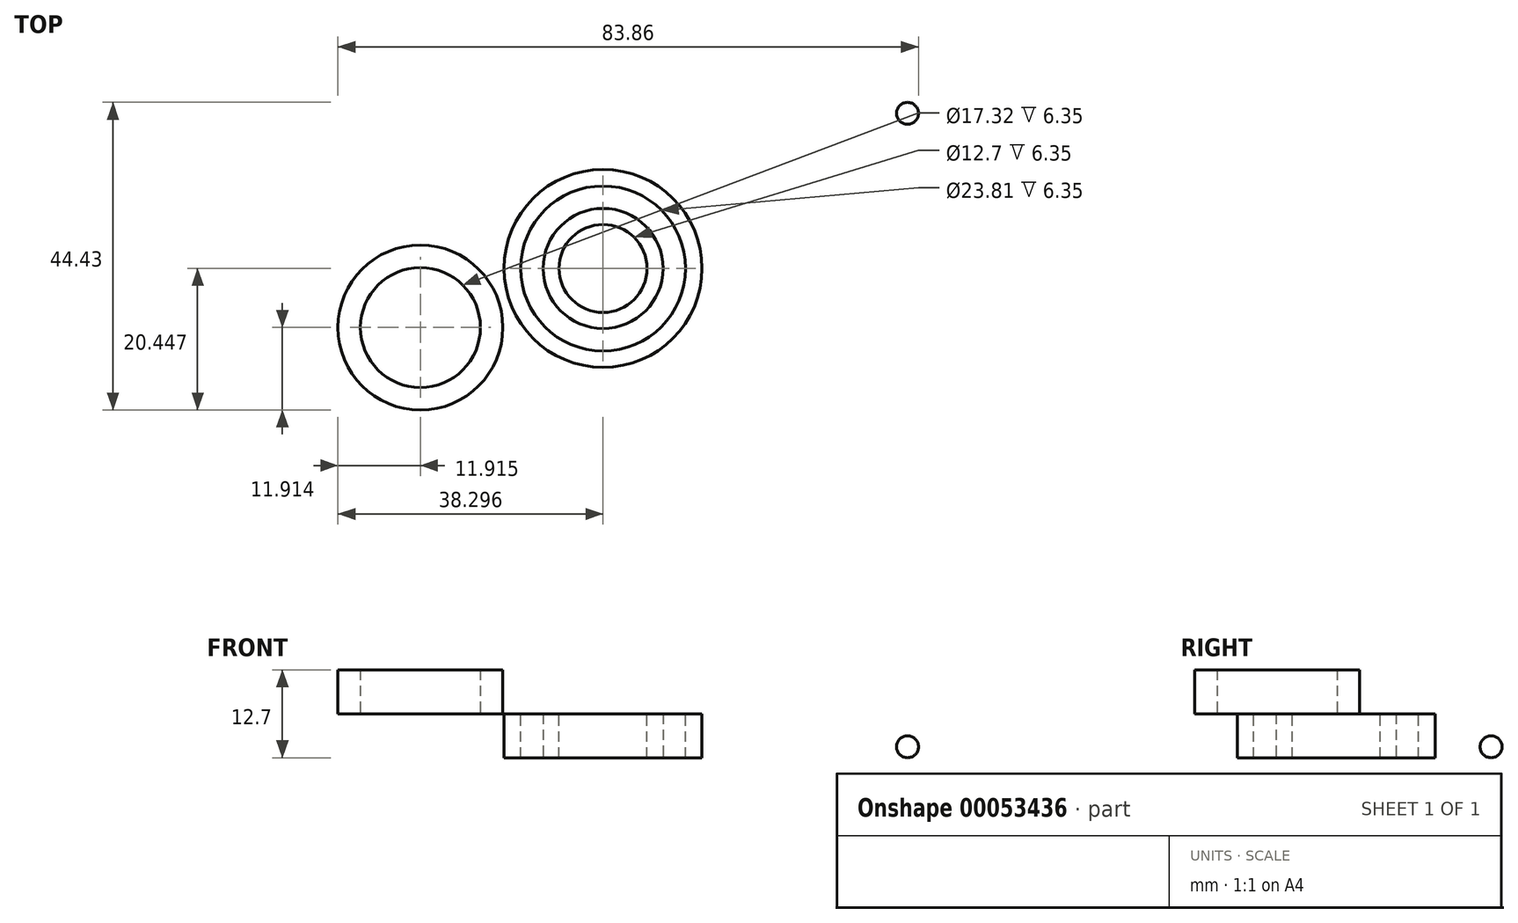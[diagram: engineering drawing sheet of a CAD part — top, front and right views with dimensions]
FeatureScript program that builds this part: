
annotation { "Feature Type Name" : "Feature", "Feature Type Description" : "" }
export const myFeature = defineFeature(function(context is Context, id is Id, definition is map)
    precondition{}
    {
        {
            var Q0;
            Q0=qCreatedBy(makeId("Top.planeOp"),FACE);
            var sketch = newSketch(context, id + "F0", { "sketchPlane" : qUnion([Q0])});
            skCircle(sketch, "E0", {"center": v(-43.97, -22.4) * mm, "radius": 14.29 * mm});
            skSolve(sketch);
        }
        {
            var Q0;
            Q0=makeQuery(id+"F0.imprint","IMPRINT",FACE,{"disambiguationData":[TD([[makeQuery(id+"F0.imprint","IMPRINT",EDGE,{"derivedFrom":sQuery(id+"F0.wireOp",EDGE,"E0")}),1.0]])]});
            extrude(context, id + "F1", {"entities" : qUnion([Q0]), "depth" : 6.35 * mm});
        }
        {
            var Q0;
            Q0=makeQuery(id+"F1.opExtrude","CAP_FACE",FACE,{"disambiguationData":[OSD([sQuery(id+"F0.wireOp",EDGE,"E0")])],"isStart":false});
            var sketch = newSketch(context, id + "F2", { "sketchPlane" : qUnion([Q0])});
            skPoint(sketch, "E1", {"position": v(-43.97, -22.4) * mm});
            skSolve(sketch);
        }
        {
            var Q0;
            Q0=sQuery(id+"F2.wireOp",VERTEX,"E1");
            var Q1;
            Q1=makeQuery(id+"F1.opExtrude","SWEPT_BODY",BODY,{"disambiguationData":[OSD([sQuery(id+"F0.wireOp",EDGE,"E0")])]});
            hole(context, id + "F3", {"style" : HoleStyle.SIMPLE, "holeDiameter" : 23.8 * mm, "endStyle" : HoleEndStyle.THROUGH, "locations" : qUnion([Q0]), "scope" : qUnion([Q1])});
        }
        {
            var Q0;
            Q0=qCreatedBy(makeId("Top.planeOp"),FACE);
            var sketch = newSketch(context, id + "F4", { "sketchPlane" : qUnion([Q0])});
            skCircle(sketch, "E2", {"center": v(-43.97, -22.4) * mm, "radius": 8.66 * mm});
            skSolve(sketch);
        }
        {
            var Q0;
            Q0=makeQuery(id+"F4.imprint","IMPRINT",FACE,{"disambiguationData":[TD([[makeQuery(id+"F4.imprint","IMPRINT",EDGE,{"derivedFrom":sQuery(id+"F4.wireOp",EDGE,"E2")}),1.0]])]});
            extrude(context, id + "F5", {"entities" : qUnion([Q0]), "depth" : 6.35 * mm});
        }
        {
            var Q0;
            Q0=makeQuery(id+"F5.opExtrude","CAP_FACE",FACE,{"disambiguationData":[OSD([sQuery(id+"F4.wireOp",EDGE,"E2")])],"isStart":false});
            var sketch = newSketch(context, id + "F6", { "sketchPlane" : qUnion([Q0])});
            skPoint(sketch, "E3", {"position": v(-43.97, -22.4) * mm});
            skSolve(sketch);
        }
        {
            var Q0;
            Q0=sQuery(id+"F6.wireOp",VERTEX,"E3");
            var Q1;
            Q1=makeQuery(id+"F5.opExtrude","SWEPT_BODY",BODY,{"disambiguationData":[OSD([sQuery(id+"F4.wireOp",EDGE,"E2")])]});
            hole(context, id + "F7", {"style" : HoleStyle.SIMPLE, "holeDiameter" : 12.7 * mm, "endStyle" : HoleEndStyle.THROUGH, "locations" : qUnion([Q0]), "scope" : qUnion([Q1])});
        }
        {
            var Q0;
            Q0=qCreatedBy(makeId("Top.planeOp"),FACE);
            var sketch = newSketch(context, id + "F8", { "sketchPlane" : qUnion([Q0])});
            skCircle(sketch, "E4", {"center": v(0, 0) * mm, "radius": 1.59 * mm});
            skSolve(sketch);
        }
        {
            var Q0;
            Q0 = qSketchRegion(id + "F8", true);
            extrude(context, id + "F9", {"entities" : qUnion([Q0]), "depth" : 3.17 * mm});
        }
        {
            var Q0;
            Q0=makeQuery(id+"F9.opExtrude","CAP_EDGE",EDGE,{"disambiguationData":[OSD([sQuery(id+"F8.wireOp",EDGE,"E4")])],"isStart":false});
            var Q1;
            Q1=makeQuery(id+"F9.opExtrude","CAP_EDGE",EDGE,{"disambiguationData":[OSD([sQuery(id+"F8.wireOp",EDGE,"E4")])],"isStart":true});
            fillet(context, id + "F10", {"entities" : qUnion([Q0, Q1]), "radius" : 1.59 * mm, "tangentPropagation" : true, "allowEdgeOverflow" : false});
        }
        {
            var Q0;
            Q0=makeQuery(id+"F1.opExtrude","CAP_FACE",FACE,{"disambiguationData":[OSD([sQuery(id+"F0.wireOp",EDGE,"E0")])],"isStart":false});
            var sketch = newSketch(context, id + "F11", { "sketchPlane" : qUnion([Q0])});
            skCircle(sketch, "E5", {"center": v(-70.36, -30.93) * mm, "radius": 11.91 * mm});
            skSolve(sketch);
        }
        {
            var Q0;
            Q0=makeQuery(id+"F11.imprint","IMPRINT",FACE,{"disambiguationData":[TD([[makeQuery(id+"F11.imprint","IMPRINT",EDGE,{"derivedFrom":sQuery(id+"F11.wireOp",EDGE,"E5")}),1.0]])]});
            extrude(context, id + "F12", {"entities" : qUnion([Q0]), "depth" : 6.35 * mm});
        }
        {
            var Q0;
            Q0=sQuery(id+"F11.wireOp",VERTEX,"E5.center");
            var Q1;
            Q1=makeQuery(id+"F12.opExtrude","SWEPT_BODY",BODY,{"disambiguationData":[OSD([sQuery(id+"F11.wireOp",EDGE,"E5")])]});
            hole(context, id + "F13", {"style" : HoleStyle.SIMPLE, "holeDiameter" : 17.32 * mm, "endStyle" : HoleEndStyle.THROUGH, "oppositeDirection" : true, "locations" : qUnion([Q0]), "scope" : qUnion([Q1])});
        }
    });
